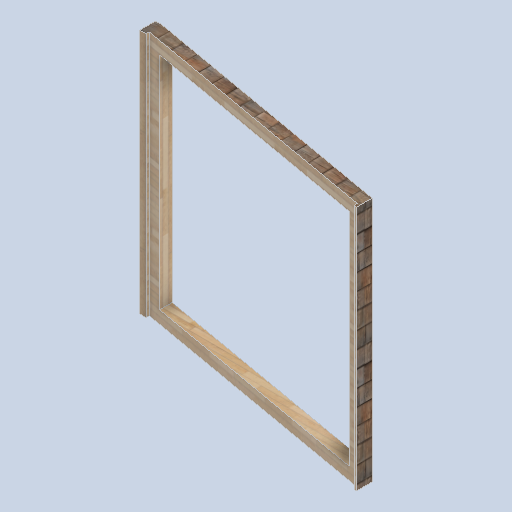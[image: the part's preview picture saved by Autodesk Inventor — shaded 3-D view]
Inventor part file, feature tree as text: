
AUTODESK INVENTOR PART (.ipt)
format: ipt  version: 2024.2 (Build 282272000, 272)  size: 182,272 bytes
history: native  units: in
note: dims shown in document units (in); Inventor stores cm internally (conversion verified against a paired STEP export)
features: plane x4, other x3, sketch x3
ambient origin geometry x8: Origin, YZ Plane, XZ Plane, XY Plane, X Axis, Y Axis, Z Axis, Center Point
bodies: Solid1 (feature_tree)
feature tree (10):
  other  "eave_frame_side_.ipt"
  other  "Solid1::eave_frame_side_.ipt"
  other  "TaggingFeature1"
  sketch  "Sketch1"  dims[d0=0.3937in]
  sketch  "Sketch6"
  sketch  "Sketch11"
  plane  "Work Plane1"
  plane  "Work Plane2"
  plane  "Work Plane3"
  plane  "Work Plane4"
